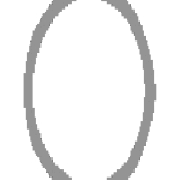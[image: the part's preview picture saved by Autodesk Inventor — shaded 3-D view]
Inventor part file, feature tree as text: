
AUTODESK INVENTOR PART (.ipt)
format: ipt  version: 2021 (Build 250183000, 183)  size: 109,568 bytes
history: native  units: in
note: dims shown in document units (in); Inventor stores cm internally (conversion verified against a paired STEP export)
features: other x4, sketch x3, plane x1
ambient origin geometry x8: Origin, YZ Plane, XZ Plane, XY Plane, X Axis, Y Axis, Z Axis, Center Point
bodies: Solid1 (feature_tree), Body (feature_tree)
feature tree (8):
  other  "Driven Length"
  other  "Frame Generator"
  other  "Start Plane"
  other  "End Plane"
  sketch  "Sketch"  dims[d2=20.2683in d4=-0.0in d5=20.2683in d6=0.12in d7=0.0in d8=90.0deg d9=20.2683in]
  sketch  "Sketch2"  dims[d0=1.0in]
  plane  "Work Plane3"
  sketch  "Sketch3"  dims[d1=0.065in]
